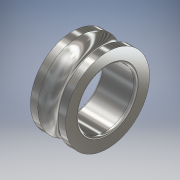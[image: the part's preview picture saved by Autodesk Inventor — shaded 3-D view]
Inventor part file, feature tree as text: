
AUTODESK INVENTOR PART (.ipt)
format: ipt  version: 2018 (Build 220112000, 112)  size: 169,472 bytes
history: native  units: mm
features: revolve x1, fillet x1, sketch x1
ambient origin geometry x8: Origin, YZ Plane, XZ Plane, XY Plane, X Axis, Y Axis, Z Axis, Center Point
bodies: Solid1 (feature_tree)
feature tree (3):
  revolve  "Revolution1"  [1 undecoded]
  fillet  "Fillet1"  Radius=15.5mm
  sketch  "Sketch1"  dims[d0=31.0mm d1=12.0mm d2=15.5mm d3=25.0mm d4=8.0mm d5=12.0mm d6=90.0deg d7=2.1mm]
note: 1 required parameter value undecoded (feature->parameter linkage not recoverable at this tier; creation-order binding heuristic only, values carry confidence <= 0.55)
